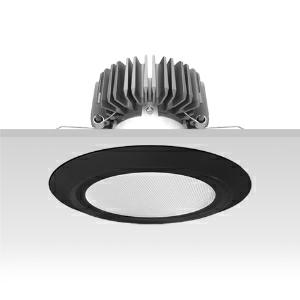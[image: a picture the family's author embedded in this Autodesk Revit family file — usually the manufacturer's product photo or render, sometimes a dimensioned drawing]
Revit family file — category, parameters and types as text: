
# Revit family: 3f_filippi_-_3f_reno_bianco_ampio_3f_filippi_-_30687_a01038_-_3f_reno_200_wh_4000-840_dali_wide___vs_bk_39a2
name_source: partatom
category: Lighting Fixtures
units: mm (PartAtom-declared; Revit-internal decimal feet)

## family parameters
Cut with Voids When Loaded = No
Host = Face
Light Source = No
Part Type = Normal
Room Calculation Point = No
Round Connector Dimension = Use Diameter
Shared = No

## types (1)
- 3F Filippi - 3F Reno Bianco Ampio (1 x LED, 3089 lm, 36 W, 4000 K)
    Apparent Load = 36 VA
    Approval mark = CE
    CIE Flux Codes = 75 94 99 100 100
    Color Rendering = 80
    Color Temperature = 4000 K
    Control Gear = Electronic transformer
    Default Elevation = 1800 mm
    Description = ILLUMINOTECHNICAL
Luminous efficiency 100% (DLOR 100%, ULOR 0%).
Initial luminous flux of the luminaire 3089 lm.
Direct symmetric wide distribution.
Installation Interdistance Transv.D = 1.16 x hu - Long.D = 1.14 x hu.
Tabular UGR (CIE 117 - 4H-8H; S=0.25H; 70/50/20): RUG 22.5 - 22.4.
Beam angle: 74° - 74°.
Luminous efficacy 86 lm/W.
Lifetime (L90/B10): 30000 h. (tq+25°C)
Lifetime (L85/B10): 50000 h. (tq+25°C)
Lifetime (L70/B10): 80000 h. (tq+25°C)
Sudden decreased luminous flux after 50000 hours: 0% (C0).
Photobiological safety in compliance with IEC/TR 62778: RG1 low risk, (IEC 62471).
In compliance with IEC/EN 62722-2-1 - IEC/EN 62717 standards.

SOURCE
Compact LED module 4000/840.
Energy efficiency class (UE 2019/2020 - UE 2019/2015): D.
CIE 13.3 Colour rendering index: CRI >80 (R9 <50%).
IES TM-30 Fidelity Index: Rf = 84 Rg = 95.
CCT nominal colour temperature 4000 K.
Colour initial tolerance (MacAdam): SDCM 3.
Zhaga Book 3 compliant.

MECHANICAL
Passive heat dissipator in die-casting aluminium, oversized, for optimum thermal management of the LED module.
Parabolic element with graduated/concentric rings in white polycarbonate.
Transparent external lens with glossy and satin differentiated surfaces, with a cooling and anti-insect system in methacrylate (PMMA).
Fastening spring clips in stainless steel.
Dimensions: diameter 226 mm, height 146 mm. Weight 1.83 kg.
IP44 protection degree for exposed part, IP20 for recessed part.
Mechanical strength to impacts IK06 (1 joule).
Glow-wire test resistance 650°C.

ELECTRICAL
Wiring on a separate unit.
Halogen Free DALI-2 DATI (Parts 251, 252, 253), PUSH-DIM, electronic wiring 230V-50/60Hz, power factor 0.97 at full load, THD <25%, constant output current, SELV, class II, 1 driver, 1 DALI addresse.
Power of the luminaire 36 W.
ENEC - CE.
SAFE FLICKER: PstLM=<1 and SVM=<0.4 (IEC TR 61547-1 and IEC TR 63158), to ensure a more comfortable and safe light.
Luminaire compliant with EN 60598-2-22 for power supply from a centralised emergency system CPSS (Central Power Supply System), not incorporated in the luminaire - high risk areas excluded. The default power and flux are 100% in AC and 100% in DC.
Ambient temperature from 0°C to +25°C.
Temperature class T6 max 85°C.
Relative humidity UR: <85%.

INSTALLATION
Pull-up recessed fitting.
False ceiling carving: 200 mm.
All accessories dedicated to this product are available on the Catalog and on our website www.3F-Filippi.com.

ACCESSORIES
A01038 - Anti-glare microprismatic VS moulded glass, tempered, not flammable, locked and in line with the trim, in black polycarbonate.

APPLICATIONS
Environments: architectural, commercial, exhibition areas, transit areas, corridors, shops, display windows, service areas.
In false ceilings with narrow voids.

LIGHT MANAGEMENT
Recommended minimum setting: 10%.
The luminaire, equipped with (DALI-2 DATI) driver, can be controlled manually with 3F Easy Dim technology or automatically/manually with wired or wireless DALI/D2D control systems.
The D2D driver guarantees interoperability with other devices with the same certification by making the following information available:
Device Data (Part 251), Energy Report (Part 252), Diagnosis & Maintenance (Part 253).
In electrical systems without a regulation system (manual or automatic) and DALI bus, a suitable jumper must be made on the DA-DA terminals of the appliance.

WARNING
Luminaire designed for disposal/recycling at end-of-life.
Replaceable (LED only) light source by a professional. Replaceable control gear by a professional.
    Height = 0 mm  [stored 0 ft]
    Lamp = 1 x LED
    Lamp Light Flux = 3089 lm
    Lamp Power = 36 W
    Lamp count = 1
    Length = 226 mm
    Lifetime = 50000 h
    Luminous efficacy = 86 lm/W
    Manufacturer = 3F Filippi
    ModVariant = No
    Model = 3F Filippi - 30687+A01038 - 3F Reno 200 WH 4000-840 DALI WIDE + VS BK
    Mounting Place = Ceiling
    Mounting Type = Recessed
    Number of Poles = 1
    OnlyDefault = Yes
    Power Factor = 1
    Product Name = 3F Filippi - 3F Reno Bianco Ampio
    Product group = recessed luminaire
    ProductGroupID = 4
    Protection Class = Protection class II
    Protection Degree = IP 20
    RLX_Detail_Level = 1
    RLX_Emergency_Light_Flux = 0 lm
    RLX_Emergency_Type = 0
    RLX_Emergency_Type_DB = No
    RlxData = <blob elided: 99397 chars, md5=690c5996>
    Socket = socket
    Standby Power = 0 W
    System Light Flux = 3089 lm
    System Power = 36 W
    Type Comments = Product without accessories
    Type Image = 3ffilippi_3f_reno_200_bk_vs_smp.jpg
    URL = http://relux.com
    VarID = ---
    Voltage = 0 V
    Weight = 0.00 kg
    Width = 0 mm  [stored 0 ft]

note: [stored X ft] marks values corroborated as IEEE doubles in the binary element streams (Revit-internal decimal feet)

## geometry (parser evidence)
native form markers: Blend x4, Sweep x9
no freeform markers — native parametric forms only
